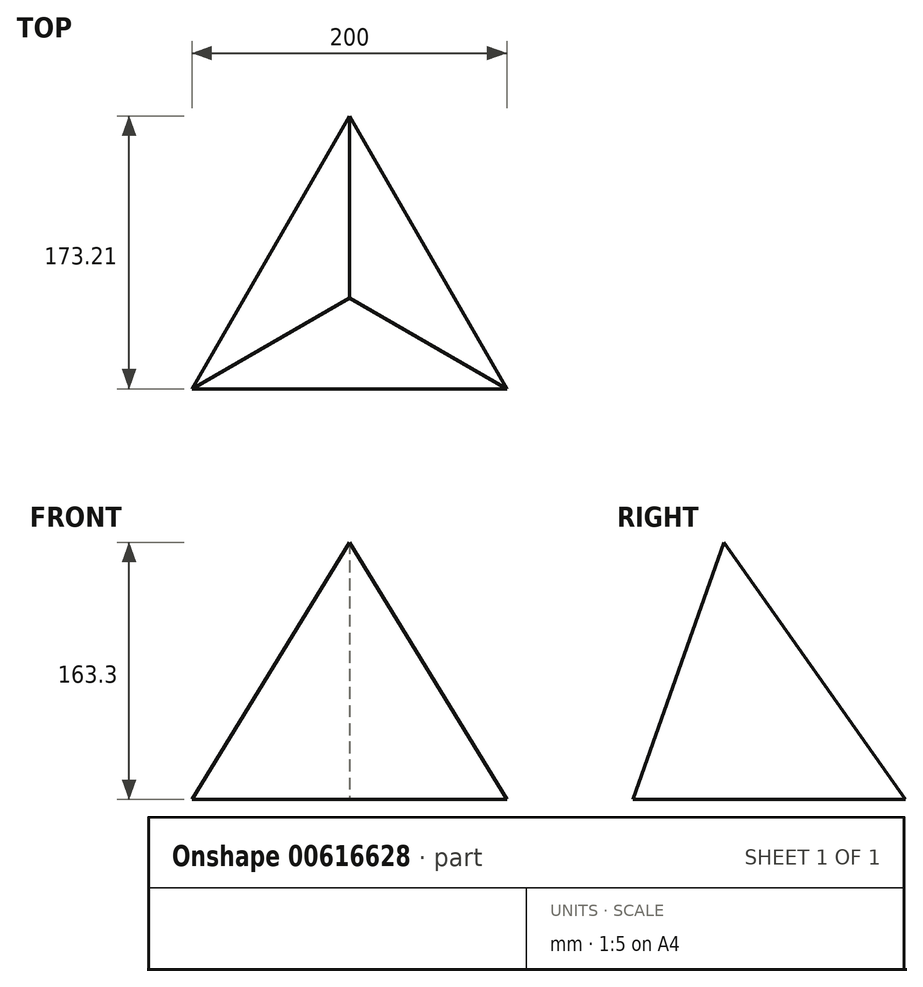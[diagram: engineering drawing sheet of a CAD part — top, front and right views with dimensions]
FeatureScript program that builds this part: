
annotation { "Feature Type Name" : "Feature", "Feature Type Description" : "" }
export const myFeature = defineFeature(function(context is Context, id is Id, definition is map)
    precondition{}
    {
        {
            var Q0;
            Q0=qCreatedBy(makeId("Top.planeOp"),FACE);
            var sketch = newSketch(context, id + "F0", { "sketchPlane" : qUnion([Q0])});
            skLineSegment(sketch, "E0", {"start": v(0, 115.47) * mm, "end": v(100, -57.74) * mm});
            skLineSegment(sketch, "E1", {"start": v(100, -57.74) * mm, "end": v(-100, -57.74) * mm});
            skLineSegment(sketch, "E2", {"start": v(-100, -57.74) * mm, "end": v(0, 115.47) * mm});
            skLineSegment(sketch, "E3", {"start": v(0, 115.47) * mm, "end": v(0, 0) * mm});
            skLineSegment(sketch, "E4", {"start": v(-100, -57.74) * mm, "end": v(0, 0) * mm});
            skLineSegment(sketch, "E5", {"start": v(0, 0) * mm, "end": v(100, -57.74) * mm});
            skPoint(sketch, "E6.orphan", {"position": v(0, -57.74) * mm});
            skLineSegment(sketch, "E7", {"start": v(0, 115.47) * mm, "end": v(0, -57.74) * mm, "construction": true});
            skSolve(sketch);
        }
        {
            assignVariable(context, id + "F1", {"name" : "Angle", "anyValue" : 70.53});
        }
        {
            var Q0;
            Q0=qSketchRegion(id+"F0",true);
            extrude(context, id + "F2", {"entities" : qUnion([Q0]), "depth" : 1000 * mm, "hasDraft" : true, "draftAngle" : (90 - getVariable(context, 'Angle')) * degree, "draftPullDirection" : true});
        }
    });
